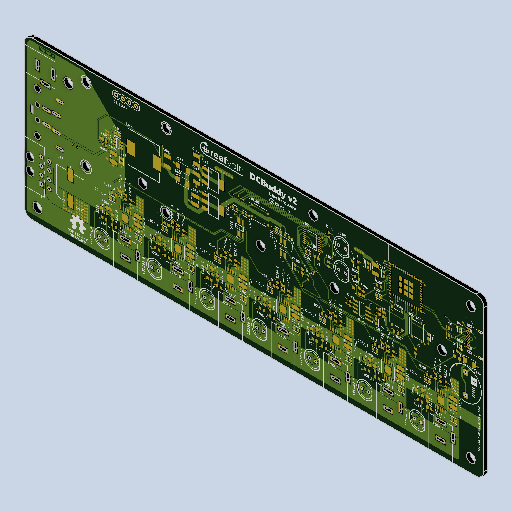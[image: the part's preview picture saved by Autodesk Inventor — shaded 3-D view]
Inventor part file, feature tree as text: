
AUTODESK INVENTOR PART (.ipt)
format: ipt  version: 2024.3 (Build 283343000, 343)  size: 2,509,824 bytes
history: native  units: in
note: dims shown in document units (in); Inventor stores cm internally (conversion verified against a paired STEP export)
features: sketch x89, hole x53, extrude x36, other x8
ambient origin geometry x8: Origin, YZ Plane, XZ Plane, XY Plane, X Axis, Y Axis, Z Axis, Center Point
bodies: Solid1 (feature_tree)
feature tree (186):
  other  "dcbuddy_v2_BOARD"
  other  "BoardFrontPlane"
  extrude  "BoardOutline"  Depth=0.13in TaperAngle=0.0deg
  hole  "LED301-C"  [1 undecoded]
  hole  "LED301-A"  [1 undecoded]
  hole  "LED300-C"  [1 undecoded]
  hole  "LED300-A"  [1 undecoded]
  hole  "LED200_CH7-C"  [1 undecoded]
  hole  "LED200_CH7-A"  [1 undecoded]
  hole  "LED200_CH6-C"  [1 undecoded]
  hole  "LED200_CH6-A"  [1 undecoded]
  hole  "LED200_CH5-C"  [1 undecoded]
  hole  "LED200_CH5-A"  [1 undecoded]
  hole  "LED200_CH4-C"  [1 undecoded]
  hole  "LED200_CH4-A"  [1 undecoded]
  hole  "LED200_CH3-C"  [1 undecoded]
  hole  "LED200_CH3-A"  [1 undecoded]
  hole  "LED200_CH2-C"  [1 undecoded]
  hole  "LED200_CH2-A"  [1 undecoded]
  hole  "LED200_CH1-C"  [1 undecoded]
  hole  "LED200_CH1-A"  [1 undecoded]
  extrude  "J701-3"  [1 undecoded]
  extrude  "J701-2"  [1 undecoded]
  extrude  "J701-1"  [1 undecoded]
  extrude  "J200_CH7-3"  [1 undecoded]
  extrude  "J200_CH7-2"  [1 undecoded]
  extrude  "J200_CH7-1"  [1 undecoded]
  extrude  "J200_CH6-3"  [1 undecoded]
  extrude  "J200_CH6-2"  [1 undecoded]
  extrude  "J200_CH6-1"  [1 undecoded]
  extrude  "J200_CH5-3"  [1 undecoded]
  extrude  "J200_CH5-2"  [1 undecoded]
  extrude  "J200_CH5-1"  [1 undecoded]
  extrude  "J200_CH4-3"  [1 undecoded]
  extrude  "J200_CH4-2"  [1 undecoded]
  extrude  "J200_CH4-1"  [1 undecoded]
  extrude  "J200_CH3-3"  [1 undecoded]
  extrude  "J200_CH3-2"  [1 undecoded]
  extrude  "J200_CH3-1"  [1 undecoded]
  extrude  "J200_CH2-3"  [1 undecoded]
  extrude  "J200_CH2-2"  [1 undecoded]
  extrude  "J200_CH2-1"  [1 undecoded]
  extrude  "J200_CH1-3"  [1 undecoded]
  extrude  "J200_CH1-2"  [1 undecoded]
  extrude  "J200_CH1-1"  [1 undecoded]
  hole  "J700-_DVCFIAIY"  [1 undecoded]
  hole  "J700-_ODLUWIDP"  [1 undecoded]
  extrude  "J700-1"  [1 undecoded]
  extrude  "J700-2"  [1 undecoded]
  extrude  "J700-3"  [1 undecoded]
  extrude  "J700-4"  [1 undecoded]
  extrude  "J700-SHLD_TGMFWFKS"  [1 undecoded]
  hole  "J700-_CQXHUJUR"  [1 undecoded]
  hole  "J700-_QRLXWSOT"  [1 undecoded]
  extrude  "J700-SHLD_YFNGGBLJ"  [1 undecoded]
  extrude  "J700-SHLD_BTUHUDDQ"  [1 undecoded]
  extrude  "J500-SH1"  [1 undecoded]
  extrude  "J500-SH2"  [1 undecoded]
  extrude  "J500-SH3"  [1 undecoded]
  extrude  "J500-SH4"  [1 undecoded]
  hole  "J500-_XJOSQWWH"  [1 undecoded]
  hole  "J500-_OTGQXOCP"  [1 undecoded]
  hole  "Free-2_QOIIXSTY"  [1 undecoded]
  hole  "Free-3"  [1 undecoded]
  hole  "Free-8"  [1 undecoded]
  hole  "Free-5"  [1 undecoded]
  hole  "Free-4"  [1 undecoded]
  hole  "Free-2_BIJDCKRQ"  [1 undecoded]
  hole  "J702-_XCDHUICF"  [1 undecoded]
  hole  "J702-_FYRNXHSV"  [1 undecoded]
  hole  "J702-4"  [1 undecoded]
  hole  "J702-3"  [1 undecoded]
  hole  "J702-2"  [1 undecoded]
  hole  "J702-1"  [1 undecoded]
  hole  "J702-5"  [1 undecoded]
  hole  "J702-6"  [1 undecoded]
  hole  "J702-7"  [1 undecoded]
  hole  "J702-8"  [1 undecoded]
  hole  "SP300--"  [1 undecoded]
  hole  "SP300-+"  [1 undecoded]
  hole  "DISP800-_EDITXKCQ"  [1 undecoded]
  hole  "DISP800-_RFTANGAA"  [1 undecoded]
  hole  "DISP800-_UQJFIAXP"  [1 undecoded]
  hole  "DISP800-4"  [1 undecoded]
  hole  "DISP800-3"  [1 undecoded]
  hole  "DISP800-2"  [1 undecoded]
  hole  "DISP800-1"  [1 undecoded]
  hole  "DISP800-_BEHFRQGU"  [1 undecoded]
  hole  "Free-7"  [1 undecoded]
  hole  "Free-6"  [1 undecoded]
  hole  "Free-2_LYDOILJT"  [1 undecoded]
  other  "Decal_Top"
  other  "Decal_Bottom"
  sketch  "Sketch1"  dims[d0=0.0559in d1=0.0in]
  sketch  "Sketch19"  dims[d111=0.032in d112=0.75in d113=0.375in d114=0.25in d115=0.5635in d116=1.0in d117=0.0in]
  sketch  "Sketch20"  dims[d118=0.032in d119=0.75in d120=0.375in d121=0.25in d122=0.5635in d123=1.0in d124=0.0in]
  sketch  "Sketch21"  dims[d125=0.032in d126=0.75in d127=0.375in d128=0.25in d129=0.5635in d130=1.0in d131=0.0in]
  sketch  "Sketch22"  dims[d132=0.032in d133=0.75in d134=0.375in d135=0.25in d136=0.5635in d137=1.0in d138=0.0in]
  sketch  "Sketch23"  dims[d139=0.032in d140=0.75in d141=0.375in d142=0.25in d143=0.5635in d144=1.0in d145=0.0in]
  sketch  "Sketch24"  dims[d146=0.032in d147=0.75in d148=0.375in d149=0.25in d150=0.5635in d151=1.0in d152=0.0in]
  sketch  "Sketch25"  dims[d153=0.032in d154=0.75in d155=0.375in d156=0.25in d157=0.5635in d158=1.0in d159=0.0in]
  sketch  "Sketch26"  dims[d160=0.032in d161=0.75in d162=0.375in d163=0.25in d164=0.5635in d165=1.0in d166=0.0in]
  sketch  "Sketch27"  dims[d167=0.032in d168=0.75in d169=0.375in d170=0.25in d171=0.5635in d172=1.0in d173=0.0in]
  sketch  "Sketch28"  dims[d174=0.032in d175=0.75in d176=0.375in d177=0.25in d178=0.5635in d179=1.0in d180=0.0in]
  sketch  "Sketch29"  dims[d181=0.032in d182=0.75in d183=0.375in d184=0.25in d185=0.5635in d186=1.0in d187=0.0in]
  sketch  "Sketch30"  dims[d188=0.032in d189=0.75in d190=0.375in d191=0.25in d192=0.5635in d193=1.0in d194=0.0in]
  sketch  "Sketch31"  dims[d195=0.032in d196=0.75in d197=0.375in d198=0.25in d199=0.5635in d200=1.0in d201=0.0in]
  sketch  "Sketch32"  dims[d202=0.032in d203=0.75in d204=0.375in d205=0.25in d206=0.5635in d207=1.0in d208=0.0in]
  sketch  "Sketch33"  dims[d209=0.032in d210=0.75in d211=0.375in d212=0.25in d213=0.5635in d214=1.0in d215=0.0in]
  sketch  "Sketch34"  dims[d216=0.032in d217=0.75in d218=0.375in d219=0.25in d220=0.5635in d221=1.0in d222=0.0in]
  sketch  "Sketch35"  dims[d223=0.032in d224=0.75in d225=0.375in d226=0.25in d227=0.5635in d228=1.0in d229=0.0in]
  sketch  "Sketch36"  dims[d230=0.032in d231=0.75in d232=0.375in d233=0.25in d234=0.5635in d235=1.0in d236=0.0in d237=0.13in d238=0.0in]
  sketch  "Sketch37"  dims[d239=0.13in d240=0.0in d241=0.13in d242=0.0in]
  sketch  "Sketch38"  dims[d243=0.13in d244=0.0in d245=0.13in d246=0.0in]
  sketch  "Sketch39"  dims[d247=0.13in d248=0.0in d249=0.13in d250=0.0in]
  sketch  "Sketch40"  dims[d251=0.13in d252=0.0in d253=0.13in d254=0.0in]
  sketch  "Sketch41"  dims[d255=0.13in d256=0.0in d257=0.13in d258=0.0in]
  sketch  "Sketch42"  dims[d259=0.13in d260=0.0in d261=0.13in d262=0.0in]
  sketch  "Sketch43"  dims[d263=0.13in d264=0.0in d265=0.13in d266=0.0in]
  sketch  "Sketch44"  dims[d267=0.13in d268=0.0in d269=0.13in d270=0.0in]
  sketch  "Sketch45"  dims[d271=0.13in d272=0.0in d273=0.13in d274=0.0in]
  sketch  "Sketch46"  dims[d275=0.13in d276=0.0in d277=0.13in d278=0.0in]
  sketch  "Sketch47"  dims[d279=0.13in d280=0.0in d281=0.13in d282=0.0in]
  sketch  "Sketch48"  dims[d283=0.13in d284=0.0in]
  sketch  "Sketch49"  dims[d285=0.0866in d286=0.75in d287=0.375in d288=0.25in d289=0.5635in d290=1.0in d291=0.0in]
  sketch  "Sketch50"  dims[d292=0.0866in d293=0.75in d294=0.375in d295=0.25in d296=0.5635in d297=1.0in d298=0.0in d299=0.13in d300=0.0in]
  sketch  "Sketch51"  dims[d301=0.13in d302=0.0in d303=0.13in d304=0.0in]
  sketch  "Sketch52"  dims[d305=0.13in d306=0.0in d307=0.13in d308=0.0in]
  sketch  "Sketch53"  dims[d309=0.0669in d310=0.75in d311=0.375in d312=0.25in d313=0.5635in d314=1.0in d315=0.0in]
  sketch  "Sketch54"  dims[d316=0.0669in d317=0.75in d318=0.375in d319=0.25in d320=0.5635in d321=1.0in d322=0.0in d323=0.13in d324=0.0in]
  sketch  "Sketch55"  dims[d325=0.13in d326=0.0in d327=0.13in d328=0.0in]
  sketch  "Sketch56"  dims[d329=0.13in d330=0.0in d331=0.13in d332=0.0in]
  sketch  "Sketch57"  dims[d333=0.13in d334=0.0in]
  sketch  "Sketch58"  dims[d335=0.0256in d336=0.75in d337=0.375in d338=0.25in d339=0.5635in d340=1.0in d341=0.0in]
  sketch  "Sketch59"  dims[d342=0.0256in d343=0.75in d344=0.375in d345=0.25in d346=0.5635in d347=1.0in d348=0.0in]
  sketch  "Sketch60"  dims[d349=0.1339in d350=0.75in d351=0.375in d352=0.25in d353=0.5635in d354=1.0in d355=0.0in]
  sketch  "Sketch61"  dims[d356=0.1339in d357=0.75in d358=0.375in d359=0.25in d360=0.5635in d361=1.0in d362=0.0in]
  sketch  "Sketch62"  dims[d363=0.1339in d364=0.75in d365=0.375in d366=0.25in d367=0.5635in d368=1.0in d369=0.0in]
  sketch  "Sketch63"  dims[d384=0.1339in d385=0.75in d386=0.375in d387=0.25in d388=0.5635in d389=1.0in d390=0.0in]
  sketch  "Sketch64"  dims[d391=0.1339in d392=0.75in d393=0.375in d394=0.25in d395=0.5635in d396=1.0in d397=0.0in]
  sketch  "Sketch65"  dims[d398=0.1339in d399=0.75in d400=0.375in d401=0.25in d402=0.5635in d403=1.0in d404=0.0in]
  sketch  "Sketch66"  dims[d409=0.1181in d410=0.75in d411=0.375in d412=0.25in d413=0.5635in d414=1.0in d415=0.0in]
  sketch  "Sketch67"  dims[d416=0.1181in d417=0.75in d418=0.375in d419=0.25in d420=0.5635in d421=1.0in d422=0.0in]
  sketch  "Sketch68"  dims[d423=0.0402in d424=0.75in d425=0.375in d426=0.25in d427=0.5635in d428=1.0in d429=0.0in]
  sketch  "Sketch69"  dims[d430=0.0402in d431=0.75in d432=0.375in d433=0.25in d434=0.5635in d435=1.0in d436=0.0in]
  sketch  "Sketch70"  dims[d437=0.0402in d438=0.75in d439=0.375in d440=0.25in d441=0.5635in d442=1.0in d443=0.0in]
  sketch  "Sketch71"  dims[d444=0.0402in d445=0.75in d446=0.375in d447=0.25in d448=0.5635in d449=1.0in d450=0.0in]
  sketch  "Sketch72"  dims[d451=0.0402in d452=0.75in d453=0.375in d454=0.25in d455=0.5635in d456=1.0in d457=0.0in]
  sketch  "Sketch73"  dims[d458=0.0402in d459=0.75in d460=0.375in d461=0.25in d462=0.5635in d463=1.0in d464=0.0in]
  sketch  "Sketch74"  dims[d465=0.0402in d466=0.75in d467=0.375in d468=0.25in d469=0.5635in d470=1.0in d471=0.0in]
  sketch  "Sketch75"  dims[d472=0.0402in d473=0.75in d474=0.375in d475=0.25in d476=0.5635in d477=1.0in d478=0.0in]
  sketch  "Sketch76"  dims[d479=0.0315in d480=0.75in d481=0.375in d482=0.25in d483=0.5635in d484=1.0in d485=0.0in]
  sketch  "Sketch77"  dims[d486=0.0315in d487=0.75in d488=0.375in d489=0.25in d490=0.5635in d491=1.0in d492=0.0in]
  sketch  "Sketch78"  dims[d497=0.12in d498=0.75in d499=0.375in d500=0.25in d501=0.5635in d502=1.0in d503=0.0in]
  sketch  "Sketch79"  dims[d504=0.12in d505=0.75in d506=0.375in d507=0.25in d508=0.5635in d509=1.0in d510=0.0in]
  sketch  "Sketch80"  dims[d511=0.12in d512=0.75in d513=0.375in d514=0.25in d515=0.5635in d516=1.0in d517=0.0in]
  sketch  "Sketch83"  dims[d518=0.04in d519=0.75in d520=0.375in d521=0.25in d522=0.5635in d523=1.0in d524=0.0in]
  sketch  "Sketch84"  dims[d525=0.04in d526=0.75in d527=0.375in d528=0.25in d529=0.5635in d530=1.0in d531=0.0in]
  sketch  "Sketch85"  dims[d532=0.04in d533=0.75in d534=0.375in d535=0.25in d536=0.5635in d537=1.0in d538=0.0in]
  sketch  "Sketch88"  dims[d539=0.04in d540=0.75in d541=0.375in d542=0.25in d543=0.5635in d544=1.0in d545=0.0in]
  sketch  "Sketch89"  dims[d546=0.12in d547=0.75in d548=0.375in d549=0.25in d550=0.5635in d551=1.0in d552=0.0in]
  sketch  "Sketch90"  dims[d553=0.1339in d554=0.75in d555=0.375in d556=0.25in d557=0.5635in d558=1.0in d559=0.0in]
  sketch  "Sketch91"  dims[d560=0.1339in d561=0.75in d562=0.375in d563=0.25in d564=0.5635in d565=1.0in d566=0.0in]
  sketch  "Sketch92"  dims[d567=0.1339in d568=0.75in d569=0.375in d570=0.25in d571=0.5635in d572=1.0in d573=0.0in d574=0.0559in]
  sketch  "Sketch93"  dims[d576=-0.0559in]
  sketch  "Sketch94"
  sketch  "Sketch95"
  sketch  "Sketch96"
  sketch  "Sketch97"
  sketch  "Sketch98"
  sketch  "Sketch99"
  sketch  "Sketch102"
  sketch  "Sketch103"
  sketch  "Sketch104"
  sketch  "Sketch105"
  sketch  "Sketch106"
  sketch  "Sketch107"
  sketch  "Sketch108"
  sketch  "Sketch109"
  sketch  "Sketch110"
  sketch  "Sketch111"
  sketch  "Sketch112"
  other  "img_Top"
  other  "G_331681337_TopDecalImage"
  other  "img_Bottom"
  other  "G_331681337_BottomDecalImage"
note: 88 required parameter values undecoded (feature->parameter linkage not recoverable at this tier; creation-order binding heuristic only, values carry confidence <= 0.55)
